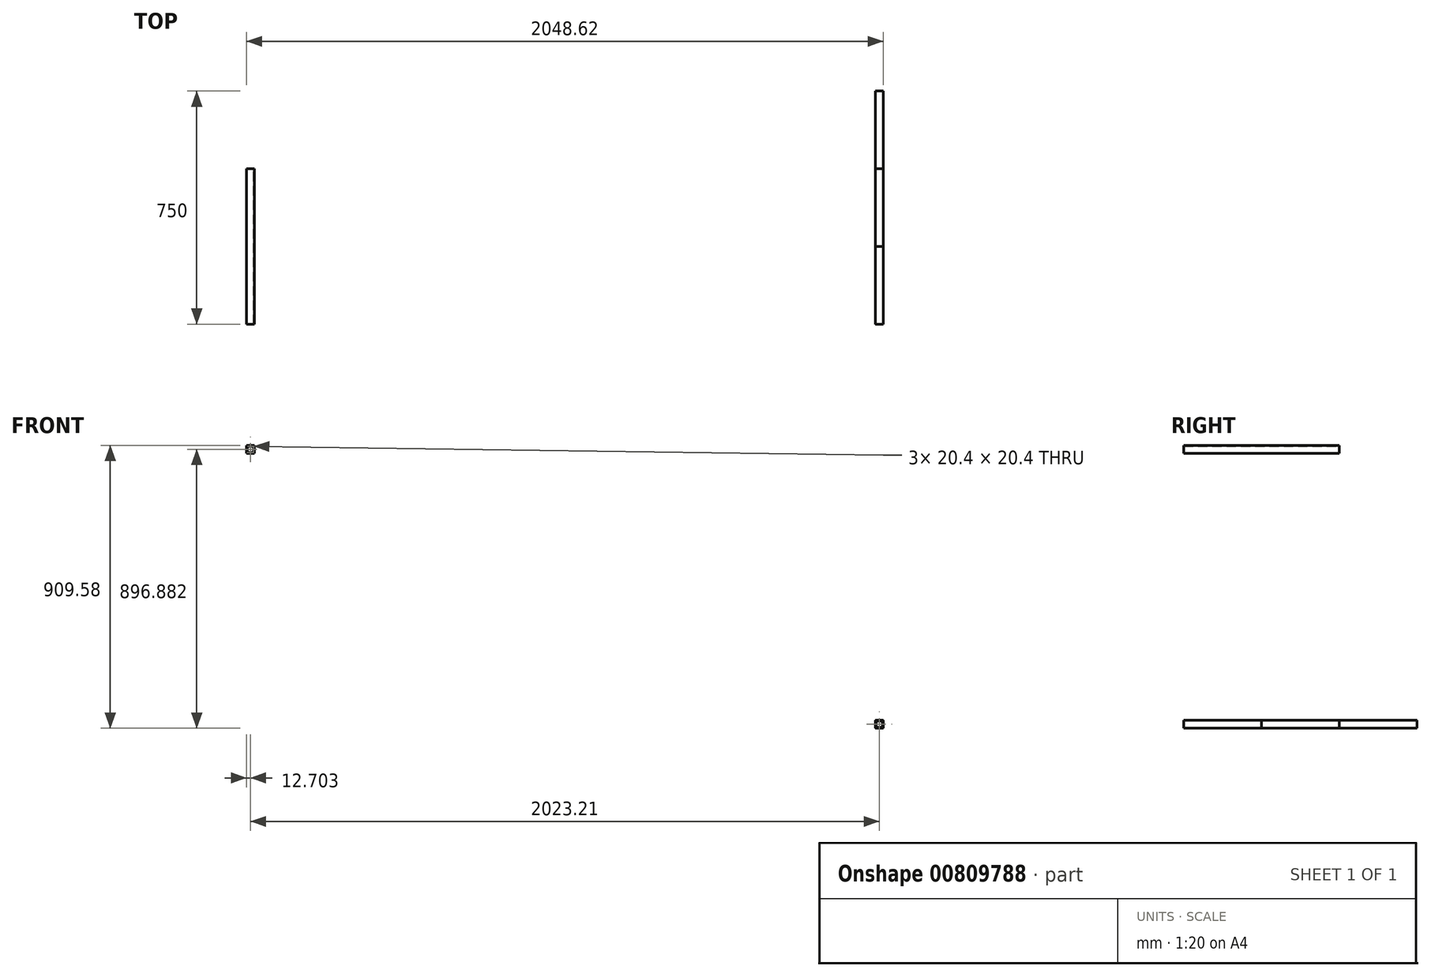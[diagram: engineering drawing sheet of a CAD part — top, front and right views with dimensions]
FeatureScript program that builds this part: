
annotation { "Feature Type Name" : "Feature", "Feature Type Description" : "" }
export const myFeature = defineFeature(function(context is Context, id is Id, definition is map)
    precondition{}
    {
        {
            var Q0;
            Q0=qCreatedBy(makeId("Front.planeOp"),FACE);
            var sketch = newSketch(context, id + "F0", { "sketchPlane" : qUnion([Q0])});
            skLineSegment(sketch, "E0.bottom", {"start": v(-12.7, 12.83) * mm, "end": v(12.7, 12.83) * mm});
            skLineSegment(sketch, "E0.top", {"start": v(-12.7, -12.57) * mm, "end": v(12.7, -12.57) * mm});
            skLineSegment(sketch, "E0.left", {"start": v(-12.7, 12.83) * mm, "end": v(-12.7, -12.57) * mm});
            skLineSegment(sketch, "E0.right", {"start": v(12.7, 12.83) * mm, "end": v(12.7, -12.57) * mm});
            skPoint(sketch, "E0.middle", {"position": v(0, 0.13) * mm});
            skLineSegment(sketch, "E1.0", {"start": v(-10.2, 10.33) * mm, "end": v(10.2, 10.33) * mm});
            skLineSegment(sketch, "E2.0", {"start": v(-10.2, 10.33) * mm, "end": v(-10.2, -10.07) * mm});
            skLineSegment(sketch, "E3.0", {"start": v(-10.2, -10.07) * mm, "end": v(10.2, -10.07) * mm});
            skLineSegment(sketch, "E4.0", {"start": v(10.2, 10.33) * mm, "end": v(10.2, -10.07) * mm});
            skSolve(sketch);
        }
        {
            var Q0;
            Q0=makeQuery(id+"F0.imprint","IMPRINT",FACE,{"disambiguationData":[TD([[makeQuery(id+"F0.imprint","IMPRINT",EDGE,{"derivedFrom":sQuery(id+"F0.wireOp",EDGE,"E0.bottom")}),-1.0]])]});
            extrude(context, id + "F1", {"entities" : qUnion([Q0]), "endBound" : BoundingType.SYMMETRIC, "depth" : 500 * mm, "offsetDistance" : 25 * mm});
        }
        {
            var Q0;
            Q0=qCreatedBy(makeId("Front.planeOp"),FACE);
            var sketch = newSketch(context, id + "F2", { "sketchPlane" : qUnion([Q0])});
            skLineSegment(sketch, "E5.bottom", {"start": v(-2035.9, 897.01) * mm, "end": v(-2010.5, 897.01) * mm});
            skLineSegment(sketch, "E5.top", {"start": v(-2035.9, 871.61) * mm, "end": v(-2010.5, 871.61) * mm});
            skLineSegment(sketch, "E5.left", {"start": v(-2035.9, 897.01) * mm, "end": v(-2035.9, 871.61) * mm});
            skLineSegment(sketch, "E5.right", {"start": v(-2010.5, 897.01) * mm, "end": v(-2010.5, 871.61) * mm});
            skPoint(sketch, "E5.middle", {"position": v(-2023.2, 884.31) * mm});
            skLineSegment(sketch, "E6.0", {"start": v(-2033.4, 894.51) * mm, "end": v(-2013, 894.51) * mm});
            skLineSegment(sketch, "E7.0", {"start": v(-2033.4, 894.51) * mm, "end": v(-2033.4, 874.11) * mm});
            skLineSegment(sketch, "E8.0", {"start": v(-2033.4, 874.11) * mm, "end": v(-2013, 874.11) * mm});
            skLineSegment(sketch, "E9.0", {"start": v(-2013, 894.51) * mm, "end": v(-2013, 874.11) * mm});
            skSolve(sketch);
        }
        {
            var Q0;
            Q0 = qSketchRegion(id + "F2", true);
            var Q1;
            Q1=makeQuery(id+"F0.imprint","IMPRINT",FACE,{"disambiguationData":[TD([[makeQuery(id+"F0.imprint","IMPRINT",EDGE,{"derivedFrom":sQuery(id+"F0.wireOp",EDGE,"E0.bottom")}),-1.0]])]});
            extrude(context, id + "F3", {"entities" : qUnion([Q0, Q1]), "depth" : 500 * mm, "offsetDistance" : 25 * mm});
        }
        {
            var Q0;
            Q0=makeQuery(id+"F3.opExtrude","SWEPT_EDGE",EDGE,{"disambiguationData":[OSD([sQuery(id+"F0.wireOp",EDGE,"E0.bottom"),sQuery(id+"F0.wireOp",EDGE,"E0.right")])]});
            var Q1;
            Q1=makeQuery(id+"F3.opExtrude","SWEPT_EDGE",EDGE,{"disambiguationData":[OSD([sQuery(id+"F0.wireOp",EDGE,"E0.top"),sQuery(id+"F0.wireOp",EDGE,"E0.right")])]});
            var Q2;
            Q2=makeQuery(id+"F3.opExtrude","SWEPT_EDGE",EDGE,{"disambiguationData":[OSD([sQuery(id+"F0.wireOp",EDGE,"E0.top"),sQuery(id+"F0.wireOp",EDGE,"E0.left")])]});
            var Q3;
            Q3=makeQuery(id+"F3.opExtrude","SWEPT_EDGE",EDGE,{"disambiguationData":[OSD([sQuery(id+"F0.wireOp",EDGE,"E0.bottom"),sQuery(id+"F0.wireOp",EDGE,"E0.left")])]});
            fillet(context, id + "F4", {"entities" : qUnion([Q0, Q1, Q2, Q3]), "radius" : 1 * mm, "tangentPropagation" : true, "allowEdgeOverflow" : false});
        }
    });
